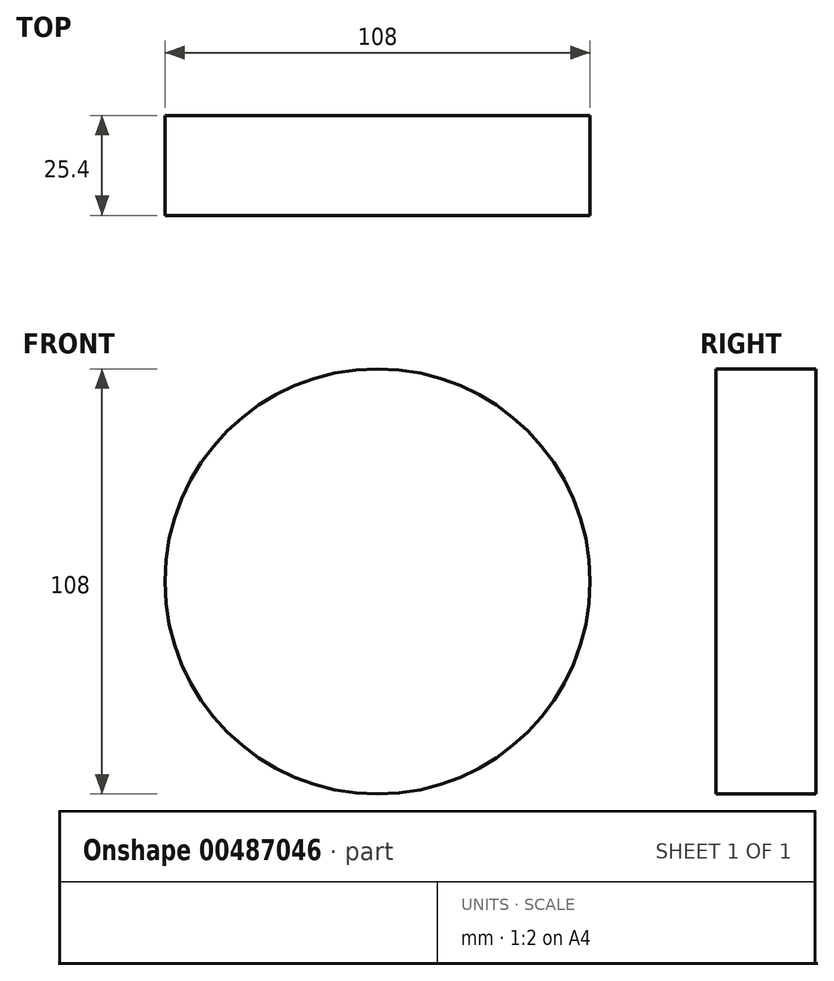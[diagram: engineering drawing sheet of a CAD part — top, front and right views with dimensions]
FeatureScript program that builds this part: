
annotation { "Feature Type Name" : "Feature", "Feature Type Description" : "" }
export const myFeature = defineFeature(function(context is Context, id is Id, definition is map)
    precondition{}
    {
        {
            var Q0;
            Q0=qCreatedBy(makeId("Front.planeOp"),FACE);
            var sketch = newSketch(context, id + "F0", { "sketchPlane" : qUnion([Q0])});
            skCircle(sketch, "E0", {"center": v(0, 0) * mm, "radius": 54 * mm});
            skSolve(sketch);
        }
        {
            var Q0;
            Q0=makeQuery(id+"F0.imprint","IMPRINT",FACE,{"disambiguationData":[TD([[makeQuery(id+"F0.imprint","IMPRINT",EDGE,{"derivedFrom":sQuery(id+"F0.wireOp",EDGE,"E0")}),1.0]])]});
            extrude(context, id + "F1", {"entities" : qUnion([Q0]), "depth" : 25.4 * mm});
        }
    });
